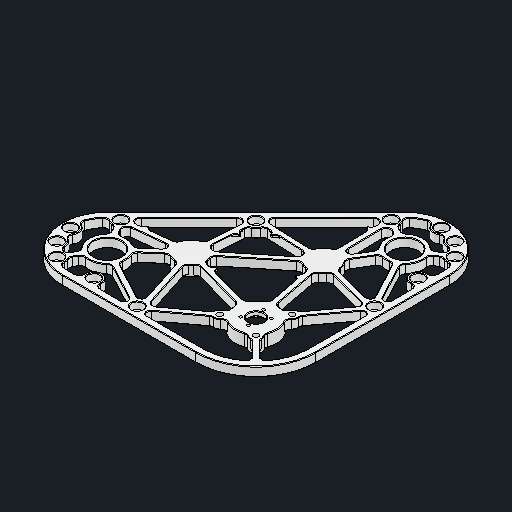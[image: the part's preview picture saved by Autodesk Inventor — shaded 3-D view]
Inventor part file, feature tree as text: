
AUTODESK INVENTOR PART (.ipt)
format: ipt  version: 2023 (Build 270158000, 158)  size: 879,104 bytes
history: native  units: in
note: dims shown in document units (in); Inventor stores cm internally (conversion verified against a paired STEP export)
features: chamfer x1
ambient origin geometry x8: Origin, YZ Plane, XZ Plane, XY Plane, X Axis, Y Axis, Z Axis, Center Point
bodies: Solid14 (feature_tree)
feature tree (1):
  chamfer  "Chamfer1"  [1 undecoded]
note: 1 required parameter value undecoded (feature->parameter linkage not recoverable at this tier; creation-order binding heuristic only, values carry confidence <= 0.55)
